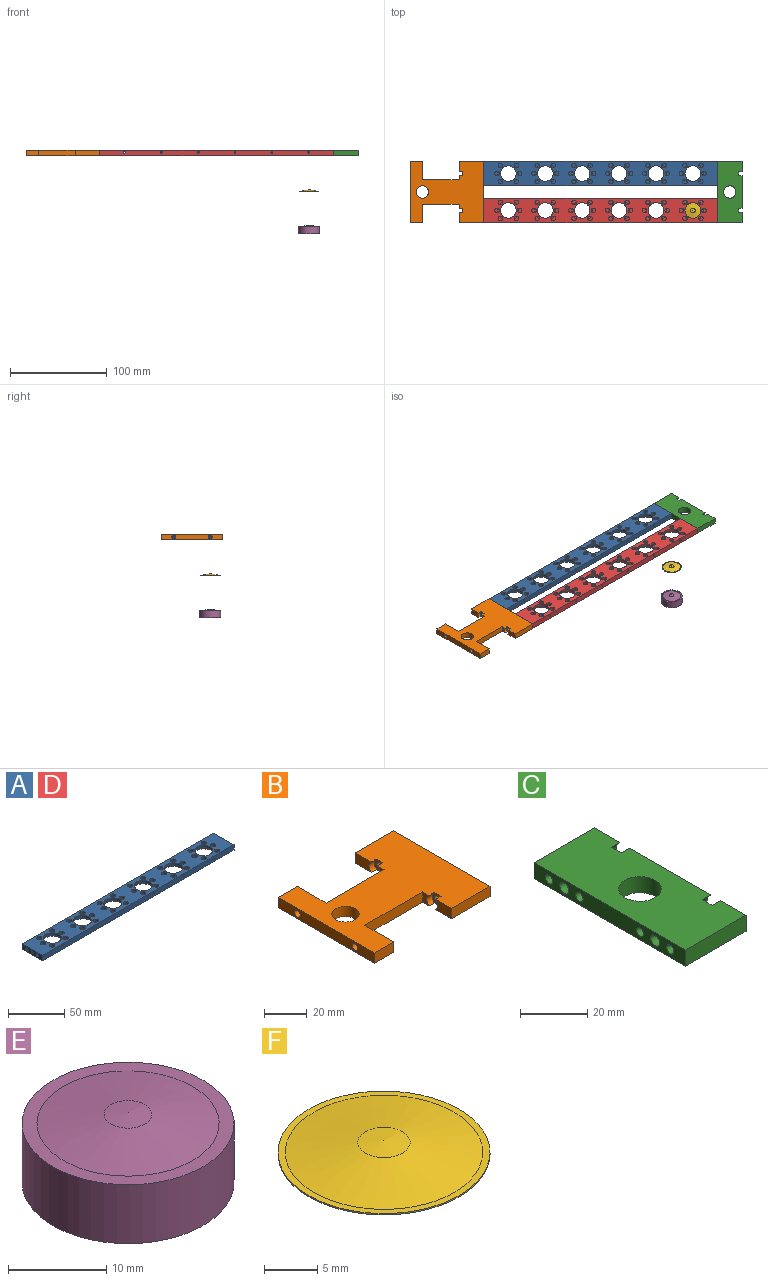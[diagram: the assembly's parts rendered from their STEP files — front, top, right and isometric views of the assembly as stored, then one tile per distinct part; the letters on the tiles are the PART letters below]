
ASSEMBLY  parts=6 mates=5
PART A: 138 faces, bbox 241.3x25.4x5.8 mm
  f0: plane 4.76x4.76mm, normal (0,0,1), area 17.8mm2, adj f1
  f1: cylinder r=2.38mm len=4.76mm, axis (0,0,1), area 38.4mm2, adj f0,f105
  f2: plane 4.76x4.76mm, normal (0,0,1), area 17.8mm2, adj f3
  f3: cylinder r=2.38mm len=4.76mm, axis (0,0,1), area 38.4mm2, adj f2,f105
  f4: plane 4.76x4.76mm, normal (0,0,1), area 17.8mm2, adj f5
  f5: cylinder r=2.38mm len=4.76mm, axis (0,0,1), area 38.4mm2, adj f4,f105
  f6: plane 4.76x4.76mm, normal (0,0,1), area 17.8mm2, adj f7
  f7: cylinder r=2.38mm len=4.76mm, axis (0,0,1), area 38.4mm2, adj f6,f105
  f8: plane 4.76x4.76mm, normal (0,0,1), area 17.8mm2, adj f9
  f9: cylinder r=2.38mm len=4.76mm, axis (0,0,1), area 38.4mm2, adj f8,f105
  f10: plane 4.76x4.76mm, normal (0,0,1), area 17.8mm2, adj f11
  f11: cylinder r=2.38mm len=4.76mm, axis (0,0,1), area 38.4mm2, adj f10,f105
  f12: cylinder r=8.1mm len=16.21mm, axis (0,0,1), area 128.8mm2, adj f13,f14,f16,f18,f105
  f13: cylinder r=0.99mm len=4.66mm, axis (0,-1,0), area 24mm2, adj f12,f14,f15,f17,f18,f19,f108
  f14: cone r=9.28mm half-angle=80.5deg, axis (0,0,-1), area 30.8mm2, adj f12,f13,f15,f16
  f15: plane 21.64x10.11mm, normal (0,0,-1), area 47.1mm2, adj f13,f14,f16,f17
  f16: cylinder r=0.99mm len=4.66mm, axis (0,-1,0), area 24mm2, adj f12,f14,f15,f17,f18,f19,f107
  f17: cylinder r=10.85mm len=21.69mm, axis (0,0,1), area 205mm2, adj f13,f15,f16,f19,f103
  f18: cone r=9.28mm half-angle=80.5deg, axis (0,0,-1), area 30.8mm2, adj f12,f13,f16,f19
  f19: plane 21.64x10.11mm, normal (0,0,-1), area 47.1mm2, adj f13,f16,f17,f18
  f20: plane 4.76x4.76mm, normal (0,0,1), area 17.8mm2, adj f21
  f21: cylinder r=2.38mm len=4.76mm, axis (0,0,1), area 38.4mm2, adj f20,f105
  f22: plane 4.76x4.76mm, normal (0,0,1), area 17.8mm2, adj f23
  f23: cylinder r=2.38mm len=4.76mm, axis (0,0,1), area 38.4mm2, adj f22,f105
  f24: plane 4.76x4.76mm, normal (0,0,1), area 17.8mm2, adj f25
  f25: cylinder r=2.38mm len=4.76mm, axis (0,0,1), area 38.4mm2, adj f24,f105
  f26: plane 4.76x4.76mm, normal (0,0,1), area 17.8mm2, adj f27
  f27: cylinder r=2.38mm len=4.76mm, axis (0,0,1), area 38.4mm2, adj f26,f105
  f28: plane 4.76x4.76mm, normal (0,0,1), area 17.8mm2, adj f29
  f29: cylinder r=2.38mm len=4.76mm, axis (0,0,1), area 38.4mm2, adj f28,f105
  f30: plane 4.76x4.76mm, normal (0,0,1), area 17.8mm2, adj f31
  f31: cylinder r=2.38mm len=4.76mm, axis (0,0,1), area 38.4mm2, adj f30,f105
  f32: cylinder r=8.1mm len=16.21mm, axis (0,0,1), area 128.8mm2, adj f33,f34,f36,f38,f105
  f33: cylinder r=0.99mm len=4.66mm, axis (0,-1,0), area 24mm2, adj f32,f34,f35,f37,f38,f39,f108
  f34: cone r=9.28mm half-angle=80.5deg, axis (0,0,-1), area 30.8mm2, adj f32,f33,f35,f36
  f35: plane 21.64x10.11mm, normal (0,0,-1), area 47.1mm2, adj f33,f34,f36,f37
  f36: cylinder r=0.99mm len=4.66mm, axis (0,-1,0), area 24mm2, adj f32,f34,f35,f37,f38,f39,f107
  f37: cylinder r=10.85mm len=21.69mm, axis (0,0,1), area 205mm2, adj f33,f35,f36,f39,f103
  f38: cone r=9.28mm half-angle=80.5deg, axis (0,0,-1), area 30.8mm2, adj f32,f33,f36,f39
  f39: plane 21.64x10.11mm, normal (0,0,-1), area 47.1mm2, adj f33,f36,f37,f38
  f40: plane 4.76x4.76mm, normal (0,0,1), area 17.8mm2, adj f41
  f41: cylinder r=2.38mm len=4.76mm, axis (0,0,1), area 38.4mm2, adj f40,f105
  f42: plane 4.76x4.76mm, normal (0,0,1), area 17.8mm2, adj f43
  f43: cylinder r=2.38mm len=4.76mm, axis (0,0,1), area 38.4mm2, adj f42,f105
  f44: plane 4.76x4.76mm, normal (0,0,1), area 17.8mm2, adj f45
  f45: cylinder r=2.38mm len=4.76mm, axis (0,0,1), area 38.4mm2, adj f44,f105
  f46: plane 4.76x4.76mm, normal (0,0,1), area 17.8mm2, adj f47
  f47: cylinder r=2.38mm len=4.76mm, axis (0,0,1), area 38.4mm2, adj f46,f105
  f48: plane 4.76x4.76mm, normal (0,0,1), area 17.8mm2, adj f49
  f49: cylinder r=2.38mm len=4.76mm, axis (0,0,1), area 38.4mm2, adj f48,f105
  f50: plane 4.76x4.76mm, normal (0,0,1), area 17.8mm2, adj f51
  f51: cylinder r=2.38mm len=4.76mm, axis (0,0,1), area 38.4mm2, adj f50,f105
  f52: cylinder r=8.1mm len=16.21mm, axis (0,0,1), area 128.8mm2, adj f53,f54,f56,f58,f105
  f53: cylinder r=0.99mm len=4.66mm, axis (0,-1,0), area 24mm2, adj f52,f54,f55,f57,f58,f59,f108
  f54: cone r=9.28mm half-angle=80.5deg, axis (0,0,-1), area 30.8mm2, adj f52,f53,f55,f56
  f55: plane 21.64x10.11mm, normal (0,0,-1), area 47.1mm2, adj f53,f54,f56,f57
  f56: cylinder r=0.99mm len=4.66mm, axis (0,-1,0), area 24mm2, adj f52,f54,f55,f57,f58,f59,f107
  f57: cylinder r=10.85mm len=21.69mm, axis (0,0,1), area 205mm2, adj f53,f55,f56,f59,f103
  f58: cone r=9.28mm half-angle=80.5deg, axis (0,0,-1), area 30.8mm2, adj f52,f53,f56,f59
  f59: plane 21.64x10.11mm, normal (0,0,-1), area 47.1mm2, adj f53,f56,f57,f58
  f60: plane 4.76x4.76mm, normal (0,0,1), area 17.8mm2, adj f61
  f61: cylinder r=2.38mm len=4.76mm, axis (0,0,1), area 38.4mm2, adj f60,f105
  f62: plane 4.76x4.76mm, normal (0,0,1), area 17.8mm2, adj f63
  f63: cylinder r=2.38mm len=4.76mm, axis (0,0,1), area 38.4mm2, adj f62,f105
  f64: plane 4.76x4.76mm, normal (0,0,1), area 17.8mm2, adj f65
  f65: cylinder r=2.38mm len=4.76mm, axis (0,0,1), area 38.4mm2, adj f64,f105
  f66: plane 4.76x4.76mm, normal (0,0,1), area 17.8mm2, adj f67
  f67: cylinder r=2.38mm len=4.76mm, axis (0,0,1), area 38.4mm2, adj f66,f105
  f68: plane 4.76x4.76mm, normal (0,0,1), area 17.8mm2, adj f69
  f69: cylinder r=2.38mm len=4.76mm, axis (0,0,1), area 38.4mm2, adj f68,f105
  f70: plane 4.76x4.76mm, normal (0,0,1), area 17.8mm2, adj f71
  f71: cylinder r=2.38mm len=4.76mm, axis (0,0,1), area 38.4mm2, adj f70,f105
  f72: cylinder r=8.1mm len=16.21mm, axis (0,0,1), area 128.8mm2, adj f73,f74,f76,f78,f105
  f73: cylinder r=0.99mm len=4.66mm, axis (0,-1,0), area 24mm2, adj f72,f74,f75,f77,f78,f79,f108
  f74: cone r=9.28mm half-angle=80.5deg, axis (0,0,-1), area 30.8mm2, adj f72,f73,f75,f76
  f75: plane 21.64x10.11mm, normal (0,0,-1), area 47.1mm2, adj f73,f74,f76,f77
  f76: cylinder r=0.99mm len=4.66mm, axis (0,-1,0), area 24mm2, adj f72,f74,f75,f77,f78,f79,f107
  f77: cylinder r=10.85mm len=21.69mm, axis (0,0,1), area 205mm2, adj f73,f75,f76,f79,f103
  f78: cone r=9.28mm half-angle=80.5deg, axis (0,0,-1), area 30.8mm2, adj f72,f73,f76,f79
  f79: plane 21.64x10.11mm, normal (0,0,-1), area 47.1mm2, adj f73,f76,f77,f78
  f80: plane 4.76x4.76mm, normal (0,0,1), area 17.8mm2, adj f81
  f81: cylinder r=2.38mm len=4.76mm, axis (0,0,1), area 38.4mm2, adj f80,f105
  f82: plane 4.76x4.76mm, normal (0,0,1), area 17.8mm2, adj f83
  f83: cylinder r=2.38mm len=4.76mm, axis (0,0,1), area 38.4mm2, adj f82,f105
  f84: plane 4.76x4.76mm, normal (0,0,1), area 17.8mm2, adj f85
  f85: cylinder r=2.38mm len=4.76mm, axis (0,0,1), area 38.4mm2, adj f84,f105
  f86: plane 4.76x4.76mm, normal (0,0,1), area 17.8mm2, adj f87
  f87: cylinder r=2.38mm len=4.76mm, axis (0,0,1), area 38.4mm2, adj f86,f105
  f88: plane 4.76x4.76mm, normal (0,0,1), area 17.8mm2, adj f89
  f89: cylinder r=2.38mm len=4.76mm, axis (0,0,1), area 38.4mm2, adj f88,f105
  f90: plane 4.76x4.76mm, normal (0,0,1), area 17.8mm2, adj f91
  f91: cylinder r=2.38mm len=4.76mm, axis (0,0,1), area 38.4mm2, adj f90,f105
  f92: cylinder r=8.1mm len=16.21mm, axis (0,0,1), area 128.8mm2, adj f93,f94,f96,f98,f105
  f93: cylinder r=0.99mm len=4.66mm, axis (0,-1,0), area 24mm2, adj f92,f94,f95,f97,f98,f99,f108
  f94: cone r=9.28mm half-angle=80.5deg, axis (0,0,-1), area 30.8mm2, adj f92,f93,f95,f96
  f95: plane 21.64x10.11mm, normal (0,0,-1), area 47.1mm2, adj f93,f94,f96,f97
  f96: cylinder r=0.99mm len=4.66mm, axis (0,-1,0), area 24mm2, adj f92,f94,f95,f97,f98,f99,f107
  f97: cylinder r=10.85mm len=21.69mm, axis (0,0,1), area 205mm2, adj f93,f95,f96,f99,f103
  f98: cone r=9.28mm half-angle=80.5deg, axis (0,0,-1), area 30.8mm2, adj f92,f93,f96,f99
  f99: plane 21.64x10.11mm, normal (0,0,-1), area 47.1mm2, adj f93,f96,f97,f98
  f100: cylinder r=0.99mm len=4.66mm, axis (0,-1,0), area 24mm2, adj f101,f102,f108,f109,f110,f111,f113
  f101: cone r=9.28mm half-angle=80.5deg, axis (0,0,-1), area 30.8mm2, adj f100,f102,f112,f113
  f102: plane 21.64x10.11mm, normal (0,0,-1), area 47.1mm2, adj f100,f101,f109,f112
  f103: plane 241.3x25.4mm, normal (0,0,-1), area 3911.7mm2, adj f17,f37,f57,f77,f97,f104,f106,f107
  f104: plane 25.4x5.84mm, normal (1,0,0), area 128mm2, adj f103,f105,f107,f108,f133,f135,f137
  f105: plane 241.3x25.4mm, normal (0,0,1), area 4250.2mm2, adj f1,f3,f5,f7,f9,f11,f12,f21
  f106: plane 25.4x5.84mm, normal (-1,0,0), area 128mm2, adj f103,f105,f107,f108,f127,f129,f131
  f107: plane 241.3x5.84mm, normal (0,-1,0), area 1391.1mm2, adj f16,f36,f56,f76,f96,f103,f104,f105
  f108: plane 241.3x5.84mm, normal (0,1,0), area 1391.1mm2, adj f13,f33,f53,f73,f93,f100,f103,f104
  f109: cylinder r=10.85mm len=21.69mm, axis (0,0,1), area 205mm2, adj f100,f102,f103,f111,f112
  f110: cone r=9.28mm half-angle=80.5deg, axis (0,0,-1), area 30.8mm2, adj f100,f111,f112,f113
  f111: plane 21.64x10.11mm, normal (0,0,-1), area 47.1mm2, adj f100,f109,f110,f112
  f112: cylinder r=0.99mm len=4.66mm, axis (0,-1,0), area 24mm2, adj f101,f102,f107,f109,f110,f111,f113
  f113: cylinder r=8.1mm len=16.21mm, axis (0,0,1), area 128.8mm2, adj f100,f101,f105,f110,f112
  f114: plane 4.76x4.76mm, normal (0,0,1), area 17.8mm2, adj f115
  f115: cylinder r=2.38mm len=4.76mm, axis (0,0,1), area 38.4mm2, adj f105,f114
  f116: plane 4.76x4.76mm, normal (0,0,1), area 17.8mm2, adj f117
  f117: cylinder r=2.38mm len=4.76mm, axis (0,0,1), area 38.4mm2, adj f105,f116
  f118: plane 4.76x4.76mm, normal (0,0,1), area 17.8mm2, adj f119
  f119: cylinder r=2.38mm len=4.76mm, axis (0,0,1), area 38.4mm2, adj f105,f118
  f120: plane 4.76x4.76mm, normal (0,0,1), area 17.8mm2, adj f121
  f121: cylinder r=2.38mm len=4.76mm, axis (0,0,1), area 38.4mm2, adj f105,f120
  f122: plane 4.76x4.76mm, normal (0,0,1), area 17.8mm2, adj f123
  f123: cylinder r=2.38mm len=4.76mm, axis (0,0,1), area 38.4mm2, adj f105,f122
  f124: plane 4.76x4.76mm, normal (0,0,1), area 17.8mm2, adj f125
  f125: cylinder r=2.38mm len=4.76mm, axis (0,0,1), area 38.4mm2, adj f105,f124
  f126: cone r=0mm half-angle=59deg, axis (-1,0,0), area 8.5mm2, adj f127
  f127: cylinder r=1.52mm len=6.35mm, axis (-1,0,0), area 60.8mm2, adj f106,f126
  f128: cone r=0mm half-angle=59deg, axis (-1,0,0), area 8.5mm2, adj f129
  f129: cylinder r=1.52mm len=6.35mm, axis (-1,0,0), area 60.8mm2, adj f106,f128
  f130: cone r=0mm half-angle=59deg, axis (-1,0,0), area 6.7mm2, adj f131
  f131: cylinder r=1.35mm len=6.35mm, axis (-1,0,0), area 54mm2, adj f106,f130
  f132: cone r=0mm half-angle=59deg, axis (1,0,0), area 8.5mm2, adj f133
  f133: cylinder r=1.52mm len=6.35mm, axis (1,0,0), area 60.8mm2, adj f104,f132
  f134: cone r=0mm half-angle=59deg, axis (1,0,0), area 8.5mm2, adj f135
  f135: cylinder r=1.52mm len=6.35mm, axis (1,0,0), area 60.8mm2, adj f104,f134
  f136: cone r=0mm half-angle=59deg, axis (1,0,0), area 6.7mm2, adj f137
  f137: cylinder r=1.35mm len=6.35mm, axis (1,0,0), area 54mm2, adj f104,f136
PART B: 35 faces, bbox 76.2x63.5x5.8 mm
  f0: plane 76.2x63.5mm, normal (0,0,-1), area 3231.6mm2, adj f2,f3,f4,f5,f6,f7,f8,f9
  f1: plane 76.2x63.5mm, normal (0,0,1), area 3231.6mm2, adj f2,f3,f4,f5,f6,f7,f8,f9
  f2: plane 10.64x5.84mm, normal (-1,0,0), area 56mm2, adj f0,f1,f8,f31
  f3: plane 5.84x4.29mm, normal (-1,0,0), area 18.9mm2, adj f0,f1,f9,f32
  f4: plane 5.84x4.29mm, normal (-1,0,0), area 18.9mm2, adj f0,f1,f14,f22
  f5: plane 10.64x5.84mm, normal (-1,0,0), area 56mm2, adj f0,f1,f6,f23
  f6: plane 25.4x5.84mm, normal (0,-1,0), area 148.4mm2, adj f0,f1,f5,f7
  f7: plane 63.5x5.84mm, normal (1,0,0), area 319.1mm2, adj f0,f1,f6,f8,f18,f20,f24,f27
  f8: plane 25.4x5.84mm, normal (0,1,0), area 148.4mm2, adj f0,f1,f2,f7
  f9: plane 38.1x5.84mm, normal (0,1,0), area 222.6mm2, adj f0,f1,f3,f10
  f10: plane 19.05x5.84mm, normal (1,0,0), area 100mm2, adj f0,f1,f9,f11,f34
  f11: plane 12.7x5.84mm, normal (0,1,0), area 74.2mm2, adj f0,f1,f10,f12
  f12: plane 63.5x5.84mm, normal (-1,0,0), area 348.3mm2, adj f0,f1,f11,f15,f25,f34
  f13: cylinder r=6.35mm len=12.7mm, axis (0,0,1), area 233.1mm2, adj f0,f1
  f14: plane 38.1x5.84mm, normal (0,-1,0), area 222.6mm2, adj f0,f1,f4,f16
  f15: plane 12.7x5.84mm, normal (0,-1,0), area 74.2mm2, adj f0,f1,f12,f16
  f16: plane 19.05x5.84mm, normal (1,0,0), area 100mm2, adj f0,f1,f14,f15,f25
  f17: cone r=0mm half-angle=59deg, axis (1,0,0), area 8.5mm2, adj f18
  f18: cylinder r=1.52mm len=9.53mm, axis (1,0,0), area 91.2mm2, adj f7,f17
  f19: cone r=0mm half-angle=59deg, axis (1,0,0), area 8.5mm2, adj f20
  f20: cylinder r=1.52mm len=9.53mm, axis (1,0,0), area 91.2mm2, adj f7,f19
  f21: plane 7.14x5.84mm, normal (-1,0,0), area 25.1mm2, adj f0,f1,f22,f23,f24
  f22: cylinder r=3.57mm len=5.84mm, axis (-1,0,0), area 24mm2, adj f0,f1,f4,f21
  f23: cylinder r=3.57mm len=5.84mm, axis (-1,0,0), area 24mm2, adj f0,f1,f5,f21
  f24: cylinder r=1.9mm len=21.9mm, axis (-1,0,0), area 261.2mm2, adj f7,f21
  f25: cylinder r=1.9mm len=12.7mm, axis (1,0,0), area 151.5mm2, adj f12,f16
  f26: cone r=0mm half-angle=59deg, axis (1,0,0), area 8.5mm2, adj f27
  f27: cylinder r=1.52mm len=9.53mm, axis (1,0,0), area 91.2mm2, adj f7,f26
  f28: cone r=0mm half-angle=59deg, axis (1,0,0), area 8.5mm2, adj f29
  f29: cylinder r=1.52mm len=9.53mm, axis (1,0,0), area 91.2mm2, adj f7,f28
  f30: plane 7.14x5.84mm, normal (-1,0,0), area 25.1mm2, adj f0,f1,f31,f32,f33
  f31: cylinder r=3.57mm len=5.84mm, axis (-1,0,0), area 24mm2, adj f0,f1,f2,f30
  f32: cylinder r=3.57mm len=5.84mm, axis (-1,0,0), area 24mm2, adj f0,f1,f3,f30
  f33: cylinder r=1.9mm len=21.9mm, axis (-1,0,0), area 261.2mm2, adj f7,f30
  f34: cylinder r=1.9mm len=12.7mm, axis (1,0,0), area 151.5mm2, adj f10,f12
PART C: 25 faces, bbox 25.4x63.5x5.8 mm
  f0: plane 63.5x25.4mm, normal (0,0,-1), area 1457.4mm2, adj f1,f2,f4,f5,f6,f7,f8,f14
  f1: plane 33.99x5.84mm, normal (1,0,0), area 186.1mm2, adj f0,f3,f16,f22
  f2: plane 10.64x5.84mm, normal (1,0,0), area 56mm2, adj f0,f3,f8,f23
  f3: plane 63.5x25.4mm, normal (0,0,1), area 1457.4mm2, adj f1,f2,f4,f5,f6,f7,f8,f14
  f4: plane 10.64x5.84mm, normal (1,0,0), area 56mm2, adj f0,f3,f6,f15
  f5: plane 63.5x5.84mm, normal (-1,0,0), area 319.1mm2, adj f0,f3,f6,f8,f9,f11,f13,f17
  f6: plane 25.4x5.84mm, normal (0,-1,0), area 148.4mm2, adj f0,f3,f4,f5
  f7: cylinder r=6.35mm len=12.7mm, axis (0,0,1), area 233.1mm2, adj f0,f3
  f8: plane 25.4x5.84mm, normal (0,1,0), area 148.4mm2, adj f0,f2,f3,f5
  f9: cylinder r=1.52mm len=9.53mm, axis (-1,0,0), area 91.2mm2, adj f5,f10
  f10: cone r=0mm half-angle=59deg, axis (-1,0,0), area 8.5mm2, adj f9
  f11: cylinder r=1.52mm len=9.53mm, axis (-1,0,0), area 91.2mm2, adj f5,f12
  f12: cone r=0mm half-angle=59deg, axis (-1,0,0), area 8.5mm2, adj f11
  f13: cylinder r=1.9mm len=21.9mm, axis (1,0,0), area 261.2mm2, adj f5,f14
  f14: plane 7.14x5.84mm, normal (1,0,0), area 25.1mm2, adj f0,f3,f13,f15,f16
  f15: cylinder r=3.57mm len=5.84mm, axis (1,0,0), area 24mm2, adj f0,f3,f4,f14
  f16: cylinder r=3.57mm len=5.84mm, axis (1,0,0), area 24mm2, adj f0,f1,f3,f14
  f17: cylinder r=1.52mm len=9.53mm, axis (-1,0,0), area 91.2mm2, adj f5,f18
  f18: cone r=0mm half-angle=59deg, axis (-1,0,0), area 8.5mm2, adj f17
  f19: cylinder r=1.52mm len=9.53mm, axis (-1,0,0), area 91.2mm2, adj f5,f20
  f20: cone r=0mm half-angle=59deg, axis (-1,0,0), area 8.5mm2, adj f19
  f21: plane 7.14x5.84mm, normal (1,0,0), area 25.1mm2, adj f0,f3,f22,f23,f24
  f22: cylinder r=3.57mm len=5.84mm, axis (1,0,0), area 24mm2, adj f0,f1,f3,f21
  f23: cylinder r=3.57mm len=5.84mm, axis (1,0,0), area 24mm2, adj f0,f2,f3,f21
  f24: cylinder r=1.9mm len=21.9mm, axis (1,0,0), area 261.2mm2, adj f5,f21
PART D: same geometry as A
PART E: 5 faces, bbox 21.6x21.6x8.7 mm
  f0: cylinder r=10.79mm len=21.59mm, axis (0,0,1), area 497.9mm2, adj f1,f4
  f1: plane 21.59x21.59mm, normal (0,0,-1), area 366.1mm2, adj f0
  f2: sphere r=14.76mm, area 18.8mm2, adj f3
  f3: cone r=2.44mm half-angle=80.5deg, axis (0,0,-1), area 254.9mm2, adj f2,f4
  f4: plane 21.59x21.59mm, normal (0,0,1), area 96.1mm2, adj f0,f3
PART F: 7 faces, bbox 19.9x19.9x1.5 mm
  f0: plane 19.94x19.94mm, normal (0,0,1), area 41.5mm2, adj f2,f3
  f1: sphere r=14.91mm, area 19.2mm2, adj f2
  f2: cone r=2.46mm half-angle=80.5deg, axis (0,0,-1), area 255.2mm2, adj f0,f1
  f3: cylinder r=9.97mm len=19.94mm, axis (0,0,-1), area 9.5mm2, adj f0,f6
  f4: sphere r=14.76mm, area 18.8mm2, adj f5
  f5: cone r=2.44mm half-angle=80.5deg, axis (0,0,-1), area 254.9mm2, adj f4,f6
  f6: plane 19.94x19.94mm, normal (0,0,-1), area 42.2mm2, adj f3,f5
PLACE A t=(-76.2,38.1,-1.63)mm
PLACE B t=(-76.2,0,-1.63)mm
PLACE C t=(-76.2,0,-1.63)mm
PLACE D t=(-76.2,0,-1.63)mm
PLACE E t=(0,0,-77.68)mm
PLACE F t=(0,0,-41.16)mm
MATE fastened A.f130 <-> C.f22  axis (1,0,0) through (25.4,38.1,-2.92)mm
MATE fastened D.f130 <-> C.f13  axis (1,0,0) through (25.4,0,-2.92)mm
MATE slider D.f74 <-> F.f2  axis (0,0,1) through (0,0,-4.33)mm
MATE fastened D.f130 <-> B.f22  axis (-1,0,0) through (-215.9,0,-2.92)mm
MATE slider E.f0 <-> D.f74  axis (0,0,1) through (0,0,-79.02)mm
